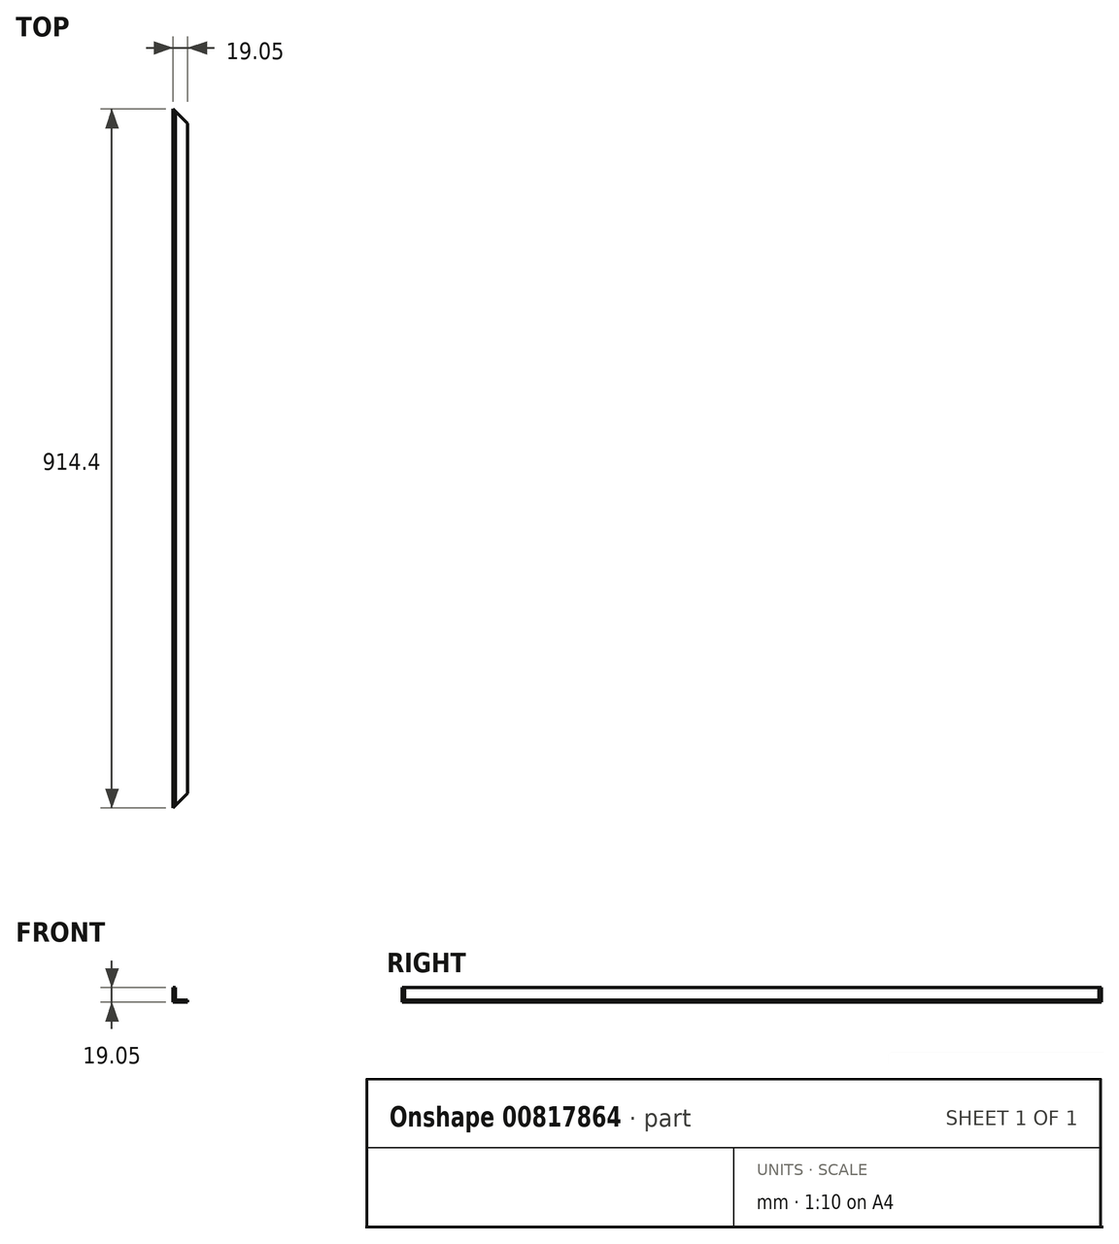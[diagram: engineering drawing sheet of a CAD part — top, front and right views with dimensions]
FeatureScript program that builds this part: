
annotation { "Feature Type Name" : "Feature", "Feature Type Description" : "" }
export const myFeature = defineFeature(function(context is Context, id is Id, definition is map)
    precondition{}
    {
        {
            var Q0;
            Q0=qCreatedBy(makeId("Front.planeOp"),FACE);
            var sketch = newSketch(context, id + "F0", { "sketchPlane" : qUnion([Q0])});
            skLineSegment(sketch, "E0", {"start": v(0, 0) * mm, "end": v(0, 19.05) * mm});
            skLineSegment(sketch, "E1", {"start": v(0, 0) * mm, "end": v(19.05, 0) * mm});
            skLineSegment(sketch, "E2.0", {"start": v(3.05, 3.05) * mm, "end": v(3.05, 19.05) * mm});
            skLineSegment(sketch, "E3.0", {"start": v(3.05, 3.05) * mm, "end": v(19.05, 3.05) * mm});
            skLineSegment(sketch, "E4", {"start": v(0, 19.05) * mm, "end": v(3.05, 19.05) * mm});
            skLineSegment(sketch, "E5", {"start": v(19.05, 0) * mm, "end": v(19.05, 3.05) * mm});
            skSolve(sketch);
        }
        {
            var Q0;
            Q0=makeQuery(id+"F0.imprint","IMPRINT",FACE,{"disambiguationData":[TD([[makeQuery(id+"F0.imprint","IMPRINT",EDGE,{"derivedFrom":sQuery(id+"F0.wireOp",EDGE,"E0")}),-1.0]])]});
            extrude(context, id + "F1", {"entities" : qUnion([Q0]), "depth" : 914.4 * mm, "offsetDistance" : 25.4 * mm});
        }
        {
            var Q0;
            Q0=makeQuery(id+"F1.opExtrude","SWEPT_FACE",FACE,{"disambiguationData":[OSD([sQuery(id+"F0.wireOp",EDGE,"E1")])]});
            var sketch = newSketch(context, id + "F2", { "sketchPlane" : qUnion([Q0])});
            skLineSegment(sketch, "E6", {"start": v(0, 914.4) * mm, "end": v(19.05, 895.35) * mm});
            skLineSegment(sketch, "E7", {"start": v(19.05, 895.35) * mm, "end": v(19.05, 914.4) * mm});
            skLineSegment(sketch, "E8", {"start": v(19.05, 914.4) * mm, "end": v(0, 914.4) * mm});
            skSolve(sketch);
        }
        {
            var Q0;
            Q0=makeQuery(id+"F2.imprint","IMPRINT",FACE,{"disambiguationData":[TD([[makeQuery(id+"F2.imprint","IMPRINT",EDGE,{"derivedFrom":sQuery(id+"F2.wireOp",EDGE,"E6")}),1.0]])]});
            extrude(context, id + "F3", {"entities" : qUnion([Q0]), "operationType" : NewBodyOperationType.REMOVE, "endBound" : BoundingType.THROUGH_ALL, "oppositeDirection" : true, "depth" : 25.4 * mm, "offsetDistance" : 25.4 * mm});
        }
        {
            var Q0;
            Q0=makeQuery(id+"F1.opExtrude","SWEPT_FACE",FACE,{"disambiguationData":[OSD([sQuery(id+"F0.wireOp",EDGE,"E1")])]});
            var sketch = newSketch(context, id + "F4", { "sketchPlane" : qUnion([Q0])});
            skLineSegment(sketch, "E9", {"start": v(0, 0) * mm, "end": v(19.05, 19.05) * mm});
            skLineSegment(sketch, "E10", {"start": v(19.05, 19.05) * mm, "end": v(19.05, 0) * mm});
            skLineSegment(sketch, "E11", {"start": v(19.05, 0) * mm, "end": v(0, 0) * mm});
            skSolve(sketch);
        }
        {
            var Q0;
            Q0=makeQuery(id+"F4.imprint","IMPRINT",FACE,{"disambiguationData":[TD([[makeQuery(id+"F4.imprint","IMPRINT",EDGE,{"derivedFrom":sQuery(id+"F4.wireOp",EDGE,"E9")}),-1.0]])]});
            extrude(context, id + "F5", {"entities" : qUnion([Q0]), "operationType" : NewBodyOperationType.REMOVE, "endBound" : BoundingType.THROUGH_ALL, "oppositeDirection" : true, "depth" : 25.4 * mm, "offsetDistance" : 25.4 * mm});
        }
    });
